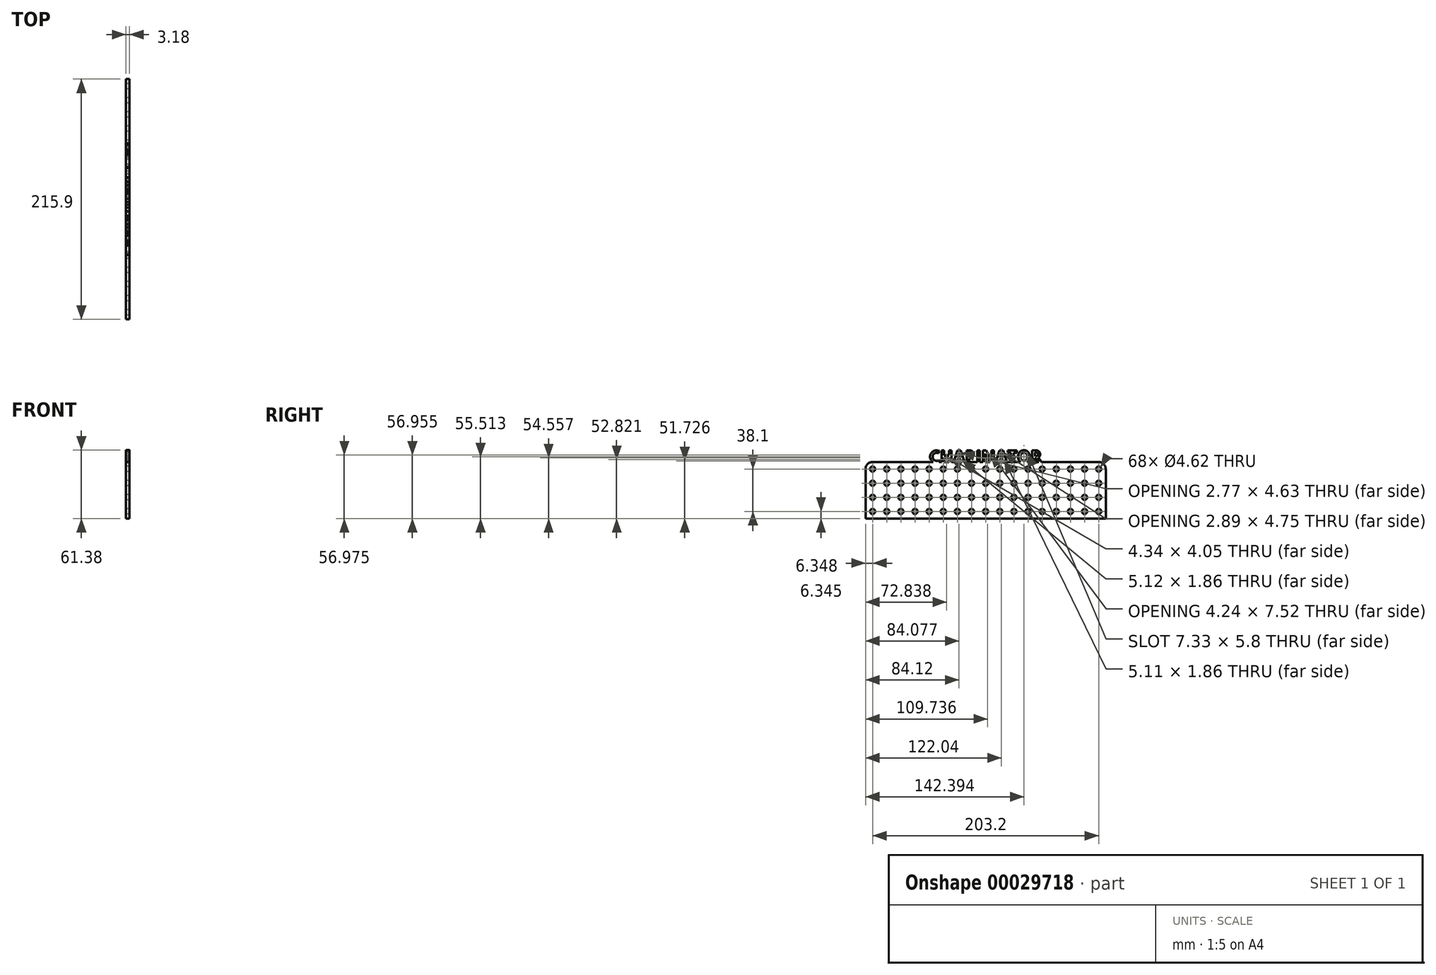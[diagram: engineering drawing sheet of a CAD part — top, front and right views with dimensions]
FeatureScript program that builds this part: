
annotation { "Feature Type Name" : "Feature", "Feature Type Description" : "" }
export const myFeature = defineFeature(function(context is Context, id is Id, definition is map)
    precondition{}
    {
        {
            var Q0;
            Q0=qCreatedBy(makeId("Right.planeOp"),FACE);
            var sketch = newSketch(context, id + "F0", { "sketchPlane" : qUnion([Q0])});
            skLineSegment(sketch, "E0.bottom", {"start": v(-117.2, -23.47) * mm, "end": v(98.7, -23.47) * mm});
            skLineSegment(sketch, "E0.top", {"start": v(-110.84, 27.33) * mm, "end": v(-56.58, 27.33) * mm});
            skLineSegment(sketch, "E0.left", {"start": v(-117.2, -23.47) * mm, "end": v(-117.2, 20.98) * mm});
            skLineSegment(sketch, "E0.right", {"start": v(98.7, -23.47) * mm, "end": v(98.7, 20.98) * mm});
            skCircle(sketch, "E1", {"center": v(-110.84, -17.12) * mm, "radius": 2.31 * mm});
            skCircle(sketch, "E2.1.0.0", {"center": v(-98.14, -17.12) * mm, "radius": 2.31 * mm});
            skCircle(sketch, "E2.2.0.0", {"center": v(-85.44, -17.12) * mm, "radius": 2.31 * mm});
            skCircle(sketch, "E2.3.0.0", {"center": v(-72.74, -17.12) * mm, "radius": 2.31 * mm});
            skCircle(sketch, "E2.4.0.0", {"center": v(-60.04, -17.12) * mm, "radius": 2.31 * mm});
            skCircle(sketch, "E2.5.0.0", {"center": v(-47.34, -17.12) * mm, "radius": 2.31 * mm});
            skCircle(sketch, "E2.6.0.0", {"center": v(-34.64, -17.12) * mm, "radius": 2.31 * mm});
            skCircle(sketch, "E2.7.0.0", {"center": v(-21.94, -17.12) * mm, "radius": 2.31 * mm});
            skCircle(sketch, "E2.8.0.0", {"center": v(-9.24, -17.12) * mm, "radius": 2.31 * mm});
            skCircle(sketch, "E2.9.0.0", {"center": v(3.46, -17.12) * mm, "radius": 2.31 * mm});
            skCircle(sketch, "E2.10.0.0", {"center": v(16.16, -17.12) * mm, "radius": 2.31 * mm});
            skCircle(sketch, "E2.11.0.0", {"center": v(28.86, -17.12) * mm, "radius": 2.31 * mm});
            skCircle(sketch, "E2.12.0.0", {"center": v(41.56, -17.12) * mm, "radius": 2.31 * mm});
            skCircle(sketch, "E2.13.0.0", {"center": v(54.26, -17.12) * mm, "radius": 2.31 * mm});
            skCircle(sketch, "E2.14.0.0", {"center": v(66.96, -17.12) * mm, "radius": 2.31 * mm});
            skCircle(sketch, "E2.15.0.0", {"center": v(79.66, -17.12) * mm, "radius": 2.31 * mm});
            skLineSegment(sketch, "E2.direction1", {"start": v(-110.84, -17.12) * mm, "end": v(-98.14, -17.12) * mm, "construction": true});
            skCircle(sketch, "E3.0.16.0", {"center": v(92.36, -17.12) * mm, "radius": 2.31 * mm});
            skCircle(sketch, "E4.1.0.0", {"center": v(-34.64, -4.42) * mm, "radius": 2.31 * mm});
            skCircle(sketch, "E4.1.0.1", {"center": v(-9.24, -4.42) * mm, "radius": 2.31 * mm});
            skCircle(sketch, "E4.1.0.2", {"center": v(-21.94, -4.42) * mm, "radius": 2.31 * mm});
            skCircle(sketch, "E4.1.0.3", {"center": v(66.96, -4.42) * mm, "radius": 2.31 * mm});
            skCircle(sketch, "E4.1.0.4", {"center": v(-47.34, -4.42) * mm, "radius": 2.31 * mm});
            skCircle(sketch, "E4.1.0.5", {"center": v(-60.04, -4.42) * mm, "radius": 2.31 * mm});
            skCircle(sketch, "E4.1.0.6", {"center": v(-72.74, -4.42) * mm, "radius": 2.31 * mm});
            skCircle(sketch, "E4.1.0.7", {"center": v(-85.44, -4.42) * mm, "radius": 2.31 * mm});
            skCircle(sketch, "E4.1.0.8", {"center": v(-98.14, -4.42) * mm, "radius": 2.31 * mm});
            skCircle(sketch, "E4.1.0.9", {"center": v(-110.84, -4.42) * mm, "radius": 2.31 * mm});
            skCircle(sketch, "E4.1.0.10", {"center": v(28.86, -4.42) * mm, "radius": 2.31 * mm});
            skCircle(sketch, "E4.1.0.11", {"center": v(16.16, -4.42) * mm, "radius": 2.31 * mm});
            skCircle(sketch, "E4.1.0.12", {"center": v(54.26, -4.42) * mm, "radius": 2.31 * mm});
            skCircle(sketch, "E4.1.0.13", {"center": v(3.46, -4.42) * mm, "radius": 2.31 * mm});
            skCircle(sketch, "E4.1.0.14", {"center": v(79.66, -4.42) * mm, "radius": 2.31 * mm});
            skCircle(sketch, "E4.1.0.15", {"center": v(92.36, -4.42) * mm, "radius": 2.31 * mm});
            skCircle(sketch, "E4.1.0.16", {"center": v(41.56, -4.42) * mm, "radius": 2.31 * mm});
            skCircle(sketch, "E4.2.0.0", {"center": v(-34.64, 8.28) * mm, "radius": 2.31 * mm});
            skCircle(sketch, "E4.2.0.1", {"center": v(-9.24, 8.28) * mm, "radius": 2.31 * mm});
            skCircle(sketch, "E4.2.0.2", {"center": v(-21.94, 8.28) * mm, "radius": 2.31 * mm});
            skCircle(sketch, "E4.2.0.3", {"center": v(66.96, 8.28) * mm, "radius": 2.31 * mm});
            skCircle(sketch, "E4.2.0.4", {"center": v(-47.34, 8.28) * mm, "radius": 2.31 * mm});
            skCircle(sketch, "E4.2.0.5", {"center": v(-60.04, 8.28) * mm, "radius": 2.31 * mm});
            skCircle(sketch, "E4.2.0.6", {"center": v(-72.74, 8.28) * mm, "radius": 2.31 * mm});
            skCircle(sketch, "E4.2.0.7", {"center": v(-85.44, 8.28) * mm, "radius": 2.31 * mm});
            skCircle(sketch, "E4.2.0.8", {"center": v(-98.14, 8.28) * mm, "radius": 2.31 * mm});
            skCircle(sketch, "E4.2.0.9", {"center": v(-110.84, 8.28) * mm, "radius": 2.31 * mm});
            skCircle(sketch, "E4.2.0.10", {"center": v(28.86, 8.28) * mm, "radius": 2.31 * mm});
            skCircle(sketch, "E4.2.0.11", {"center": v(16.16, 8.28) * mm, "radius": 2.31 * mm});
            skCircle(sketch, "E4.2.0.12", {"center": v(54.26, 8.28) * mm, "radius": 2.31 * mm});
            skCircle(sketch, "E4.2.0.13", {"center": v(3.46, 8.28) * mm, "radius": 2.31 * mm});
            skCircle(sketch, "E4.2.0.14", {"center": v(79.66, 8.28) * mm, "radius": 2.31 * mm});
            skCircle(sketch, "E4.2.0.15", {"center": v(92.36, 8.28) * mm, "radius": 2.31 * mm});
            skCircle(sketch, "E4.2.0.16", {"center": v(41.56, 8.28) * mm, "radius": 2.31 * mm});
            skLineSegment(sketch, "E4.direction1", {"start": v(-34.64, -17.12) * mm, "end": v(-34.64, -4.42) * mm, "construction": true});
            skCircle(sketch, "E5.0.3.0", {"center": v(-34.64, 20.98) * mm, "radius": 2.31 * mm});
            skCircle(sketch, "E5.2.3.0", {"center": v(-9.24, 20.98) * mm, "radius": 2.31 * mm});
            skCircle(sketch, "E5.4.3.0", {"center": v(-21.94, 20.98) * mm, "radius": 2.31 * mm});
            skCircle(sketch, "E5.6.3.0", {"center": v(66.96, 20.98) * mm, "radius": 2.31 * mm});
            skCircle(sketch, "E5.8.3.0", {"center": v(-47.34, 20.98) * mm, "radius": 2.31 * mm});
            skCircle(sketch, "E5.10.3.0", {"center": v(-60.04, 20.98) * mm, "radius": 2.31 * mm});
            skCircle(sketch, "E5.12.3.0", {"center": v(-72.74, 20.98) * mm, "radius": 2.31 * mm});
            skCircle(sketch, "E5.14.3.0", {"center": v(-85.44, 20.98) * mm, "radius": 2.31 * mm});
            skCircle(sketch, "E5.16.3.0", {"center": v(-98.14, 20.98) * mm, "radius": 2.31 * mm});
            skCircle(sketch, "E5.18.3.0", {"center": v(-110.84, 20.98) * mm, "radius": 2.31 * mm});
            skCircle(sketch, "E5.20.3.0", {"center": v(28.86, 20.98) * mm, "radius": 2.31 * mm});
            skCircle(sketch, "E5.22.3.0", {"center": v(16.16, 20.98) * mm, "radius": 2.31 * mm});
            skCircle(sketch, "E5.24.3.0", {"center": v(54.26, 20.98) * mm, "radius": 2.31 * mm});
            skCircle(sketch, "E5.26.3.0", {"center": v(3.46, 20.98) * mm, "radius": 2.31 * mm});
            skCircle(sketch, "E5.28.3.0", {"center": v(79.66, 20.98) * mm, "radius": 2.31 * mm});
            skCircle(sketch, "E5.30.3.0", {"center": v(92.36, 20.98) * mm, "radius": 2.31 * mm});
            skCircle(sketch, "E5.32.3.0", {"center": v(41.56, 20.98) * mm, "radius": 2.31 * mm});
            skPoint(sketch, "E6.visualSharp", {"position": v(-117.2, 27.33) * mm});
            skArc(sketch, "E6.filletArc", {"start": v(-110.84, 27.33) * mm, "mid": v(-115.33, 25.47) * mm, "end": v(-117.2, 20.98) * mm});
            skPoint(sketch, "E7.visualSharp", {"position": v(98.7, 27.33) * mm});
            skArc(sketch, "E7.filletArc", {"start": v(98.7, 20.98) * mm, "mid": v(96.85, 25.47) * mm, "end": v(92.36, 27.33) * mm});
            skArc(sketch, "E8", {"start": v(-50.82, 37) * mm, "mid": v(-58.4, 34.96) * mm, "end": v(-56.58, 27.33) * mm});
            skArc(sketch, "E9", {"start": v(-51.52, 35.14) * mm, "mid": v(-56.87, 31.72) * mm, "end": v(-51.15, 28.98) * mm});
            skLineSegment(sketch, "E10", {"start": v(-50.82, 37) * mm, "end": v(-51.52, 35.14) * mm});
            skLineSegment(sketch, "E11", {"start": v(-51.15, 28.98) * mm, "end": v(-51.15, 27.33) * mm});
            skLineSegment(sketch, "E12", {"start": v(-48.84, 26.56) * mm, "end": v(-48.84, 26.58) * mm});
            skLineSegment(sketch, "E13", {"start": v(-48.84, 37.66) * mm, "end": v(-46.48, 37.66) * mm});
            skLineSegment(sketch, "E14", {"start": v(-46.48, 37.66) * mm, "end": v(-46.48, 33.2) * mm});
            skLineSegment(sketch, "E15", {"start": v(-46.48, 33.2) * mm, "end": v(-42.18, 33.2) * mm});
            skLineSegment(sketch, "E16", {"start": v(-42.18, 33.2) * mm, "end": v(-42.18, 37.66) * mm});
            skLineSegment(sketch, "E17", {"start": v(-42.18, 37.66) * mm, "end": v(-39.79, 37.66) * mm});
            skLineSegment(sketch, "E18", {"start": v(-39.79, 37.66) * mm, "end": v(-39.79, 27.33) * mm});
            skLineSegment(sketch, "E19", {"start": v(-42.18, 27.33) * mm, "end": v(-42.18, 31.38) * mm});
            skLineSegment(sketch, "E20", {"start": v(-42.18, 31.38) * mm, "end": v(-46.52, 31.38) * mm});
            skLineSegment(sketch, "E21", {"start": v(-46.52, 31.38) * mm, "end": v(-46.52, 27.33) * mm});
            skLineSegment(sketch, "E22", {"start": v(-38.11, 27.33) * mm, "end": v(-34.5, 37.66) * mm});
            skLineSegment(sketch, "E23", {"start": v(-34.5, 37.66) * mm, "end": v(-31.64, 37.66) * mm});
            skLineSegment(sketch, "E24", {"start": v(-31.64, 37.66) * mm, "end": v(-28.06, 27.33) * mm});
            skLineSegment(sketch, "E25", {"start": v(-30.55, 27.33) * mm, "end": v(-31.1, 29.19) * mm});
            skLineSegment(sketch, "E26", {"start": v(-31.1, 29.19) * mm, "end": v(-35.12, 29.19) * mm});
            skLineSegment(sketch, "E27", {"start": v(-35.12, 29.19) * mm, "end": v(-35.67, 27.33) * mm});
            skLineSegment(sketch, "E28", {"start": v(-33.13, 35.8) * mm, "end": v(-34.45, 31.17) * mm});
            skLineSegment(sketch, "E29", {"start": v(-34.45, 31.17) * mm, "end": v(-31.69, 31.17) * mm});
            skLineSegment(sketch, "E30", {"start": v(-31.69, 31.17) * mm, "end": v(-33.13, 35.8) * mm});
            skLineSegment(sketch, "E31", {"start": v(-26.4, 27.33) * mm, "end": v(-26.4, 37.66) * mm});
            skLineSegment(sketch, "E32", {"start": v(-26.4, 37.66) * mm, "end": v(-24.04, 37.66) * mm});
            skLineSegment(sketch, "E33", {"start": v(-24.04, 35.68) * mm, "end": v(-24.04, 32.41) * mm});
            skLineSegment(sketch, "E34", {"start": v(-24.08, 30.5) * mm, "end": v(-24.08, 27.33) * mm});
            skArc(sketch, "E35", {"start": v(-24.04, 32.41) * mm, "mid": v(-21.3, 34.04) * mm, "end": v(-24.04, 35.68) * mm});
            skArc(sketch, "E36", {"start": v(-24.08, 30.5) * mm, "mid": v(-19.9, 34.06) * mm, "end": v(-24.04, 37.66) * mm});
            skLineSegment(sketch, "E37", {"start": v(-16.72, 37.66) * mm, "end": v(-14.37, 37.66) * mm});
            skLineSegment(sketch, "E38", {"start": v(-14.37, 37.66) * mm, "end": v(-14.4, 27.33) * mm});
            skLineSegment(sketch, "E39", {"start": v(-16.72, 27.33) * mm, "end": v(-16.72, 37.66) * mm});
            skLineSegment(sketch, "E40", {"start": v(-11.6, 37.66) * mm, "end": v(-8.75, 37.66) * mm});
            skLineSegment(sketch, "E41", {"start": v(-8.75, 37.66) * mm, "end": v(-3.91, 29.35) * mm});
            skLineSegment(sketch, "E42", {"start": v(-3.91, 29.35) * mm, "end": v(-3.91, 37.66) * mm});
            skLineSegment(sketch, "E43", {"start": v(-3.91, 37.66) * mm, "end": v(-1.85, 37.66) * mm});
            skLineSegment(sketch, "E44", {"start": v(-1.85, 37.66) * mm, "end": v(-1.85, 27.33) * mm});
            skLineSegment(sketch, "E45", {"start": v(-5.33, 27.33) * mm, "end": v(-9.57, 34.85) * mm});
            skLineSegment(sketch, "E46", {"start": v(-9.57, 34.85) * mm, "end": v(-9.57, 27.33) * mm});
            skLineSegment(sketch, "E47", {"start": v(-11.68, 27.33) * mm, "end": v(-11.6, 37.66) * mm});
            skLineSegment(sketch, "E48", {"start": v(3.36, 37.66) * mm, "end": v(-0.14, 27.33) * mm});
            skLineSegment(sketch, "E49", {"start": v(2.3, 27.33) * mm, "end": v(2.82, 29.19) * mm});
            skLineSegment(sketch, "E50", {"start": v(2.82, 29.19) * mm, "end": v(6.87, 29.19) * mm});
            skLineSegment(sketch, "E51", {"start": v(6.87, 29.19) * mm, "end": v(7.4, 27.33) * mm});
            skLineSegment(sketch, "E52", {"start": v(9.92, 27.33) * mm, "end": v(6.3, 37.66) * mm});
            skLineSegment(sketch, "E53", {"start": v(6.3, 37.66) * mm, "end": v(3.36, 37.66) * mm});
            skLineSegment(sketch, "E54", {"start": v(4.8, 35.88) * mm, "end": v(3.4, 31.13) * mm});
            skLineSegment(sketch, "E55", {"start": v(3.4, 31.13) * mm, "end": v(6.3, 31.13) * mm});
            skLineSegment(sketch, "E56", {"start": v(6.3, 31.13) * mm, "end": v(4.8, 35.88) * mm});
            skLineSegment(sketch, "E57", {"start": v(10.47, 37.66) * mm, "end": v(10.47, 35.68) * mm});
            skLineSegment(sketch, "E58", {"start": v(10.47, 35.68) * mm, "end": v(13.45, 35.63) * mm});
            skLineSegment(sketch, "E59", {"start": v(13.45, 35.63) * mm, "end": v(13.45, 27.33) * mm});
            skLineSegment(sketch, "E60", {"start": v(15.8, 27.33) * mm, "end": v(15.84, 35.63) * mm});
            skLineSegment(sketch, "E61", {"start": v(15.84, 35.63) * mm, "end": v(18.82, 35.6) * mm});
            skLineSegment(sketch, "E62", {"start": v(18.82, 35.6) * mm, "end": v(18.82, 37.66) * mm});
            skLineSegment(sketch, "E63", {"start": v(18.82, 37.66) * mm, "end": v(10.47, 37.66) * mm});
            skArc(sketch, "E64", {"start": v(30.43, 32.12) * mm, "mid": v(25.16, 37.91) * mm, "end": v(19.9, 32.12) * mm});
            skArc(sketch, "E65", {"start": v(19.9, 32.12) * mm, "mid": v(20.35, 29.43) * mm, "end": v(22.1, 27.33) * mm});
            skArc(sketch, "E66", {"start": v(28.07, 33.06) * mm, "mid": v(25.2, 35.7) * mm, "end": v(22.34, 33.06) * mm});
            skArc(sketch, "E67", {"start": v(22.3, 31.03) * mm, "mid": v(25.2, 28.38) * mm, "end": v(28.1, 31.03) * mm});
            skLineSegment(sketch, "E68", {"start": v(38.37, 31.38) * mm, "end": v(41.05, 27.33) * mm});
            skLineSegment(sketch, "E69", {"start": v(38.48, 27.33) * mm, "end": v(36.34, 30.8) * mm});
            skLineSegment(sketch, "E70", {"start": v(36.34, 30.8) * mm, "end": v(35.14, 30.8) * mm});
            skLineSegment(sketch, "E71", {"start": v(35.14, 30.8) * mm, "end": v(35.14, 27.33) * mm});
            skLineSegment(sketch, "E72", {"start": v(32.74, 27.33) * mm, "end": v(32.65, 37.66) * mm});
            skLineSegment(sketch, "E73", {"start": v(32.65, 37.66) * mm, "end": v(35.1, 37.66) * mm});
            skLineSegment(sketch, "E74", {"start": v(35.1, 35.68) * mm, "end": v(35.1, 32.78) * mm});
            skArc(sketch, "E75", {"start": v(35.1, 32.78) * mm, "mid": v(37.8, 34.23) * mm, "end": v(35.1, 35.68) * mm});
            skArc(sketch, "E76", {"start": v(38.37, 31.38) * mm, "mid": v(39.37, 35.82) * mm, "end": v(35.23, 37.7) * mm});
            skLineSegment(sketch, "E77.trimOffspring", {"start": v(-46.52, 27.33) * mm, "end": v(-42.18, 27.33) * mm});
            skLineSegment(sketch, "E78.trimOffspring", {"start": v(-35.67, 27.33) * mm, "end": v(-30.55, 27.33) * mm});
            skLineSegment(sketch, "E79.trimOffspring", {"start": v(-28.06, 27.33) * mm, "end": v(-26.4, 27.33) * mm});
            skLineSegment(sketch, "E80.trimOffspring", {"start": v(-24.08, 27.33) * mm, "end": v(-16.72, 27.33) * mm});
            skLineSegment(sketch, "E81.trimOffspring", {"start": v(-9.57, 27.33) * mm, "end": v(-5.33, 27.33) * mm});
            skLineSegment(sketch, "E82.trimOffspring", {"start": v(35.14, 27.33) * mm, "end": v(38.48, 27.33) * mm});
            skLineSegment(sketch, "E83.trimOffspring", {"start": v(15.8, 27.33) * mm, "end": v(22.1, 27.33) * mm});
            skLineSegment(sketch, "E84.trimOffspring", {"start": v(9.92, 27.33) * mm, "end": v(13.45, 27.33) * mm});
            skLineSegment(sketch, "E85.trimOffspring", {"start": v(2.3, 27.33) * mm, "end": v(7.4, 27.33) * mm});
            skLineSegment(sketch, "E86.trimOffspring", {"start": v(-1.85, 27.33) * mm, "end": v(-0.14, 27.33) * mm});
            skLineSegment(sketch, "E87", {"start": v(-51.15, 27.33) * mm, "end": v(-48.84, 27.33) * mm});
            skLineSegment(sketch, "E88.trimOffspring", {"start": v(-39.79, 27.33) * mm, "end": v(-38.11, 27.33) * mm});
            skLineSegment(sketch, "E89", {"start": v(-14.4, 27.33) * mm, "end": v(-11.68, 27.33) * mm});
            skLineSegment(sketch, "E90", {"start": v(28.24, 27.33) * mm, "end": v(32.74, 27.33) * mm});
            skLineSegment(sketch, "E91.trimOffspring", {"start": v(41.05, 27.33) * mm, "end": v(92.36, 27.33) * mm});
            skPoint(sketch, "E92.orphan", {"position": v(-51.15, 27) * mm});
            skLineSegment(sketch, "E93.trimOffspring", {"start": v(-48.84, 27.33) * mm, "end": v(-48.84, 37.66) * mm});
            skArc(sketch, "E94.trimOffspring", {"start": v(28.24, 27.33) * mm, "mid": v(29.97, 29.43) * mm, "end": v(30.43, 32.12) * mm});
            skLineSegment(sketch, "E95", {"start": v(35.23, 37.7) * mm, "end": v(35.1, 37.66) * mm});
            skLineSegment(sketch, "E96", {"start": v(22.34, 33.06) * mm, "end": v(22.3, 31.03) * mm});
            skLineSegment(sketch, "E97", {"start": v(28.07, 33.06) * mm, "end": v(28.1, 31.03) * mm});
            skPoint(sketch, "E98.orphan", {"position": v(28, 32.12) * mm});
            skPoint(sketch, "E99.orphan", {"position": v(22.41, 32.12) * mm});
            skSolve(sketch);
        }
        {
            var Q0;
            Q0=makeQuery(id+"F0.imprint","IMPRINT",FACE,{"disambiguationData":[TD([[makeQuery(id+"F0.imprint","IMPRINT",EDGE,{"derivedFrom":sQuery(id+"F0.wireOp",EDGE,"E0.bottom")}),1.0]])]});
            extrude(context, id + "F1", {"entities" : qUnion([Q0]), "depth" : 3.17 * mm});
        }
    });
